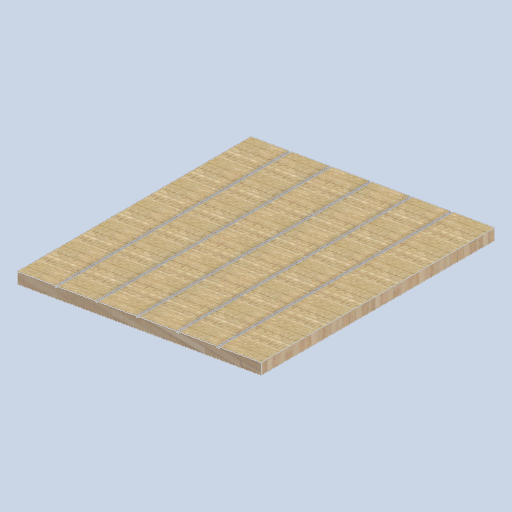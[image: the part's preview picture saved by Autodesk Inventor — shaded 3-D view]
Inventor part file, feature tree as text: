
AUTODESK INVENTOR PART (.ipt)
format: ipt  version: 2024.2 (Build 282272000, 272)  size: 427,520 bytes
history: native  units: mm
features: sketch x4, plane x3, extrude x2
ambient origin geometry x8: Origin, YZ Plane, XZ Plane, XY Plane, X Axis, Y Axis, Z Axis, Center Point
bodies: Solid1 (feature_tree)
feature tree (9):
  sketch  "Sketch1"  dims[d0=100.0mm d1=2108.0mm]
  plane  "Work Plane2"
  sketch  "Sketch2"  dims[d2=2200.0mm d3=13.962634mm]
  plane  "Work Plane3"
  extrude  "Extrusion1"  Depth=2108.0mm
  extrude  "Extrusion2"  Depth=2200.0mm
  plane  "Work Plane1"
  sketch  "Sketch3"  dims[d4=13.962634mm]
  sketch  "Sketch4"  dims[d5=2108.0mm d6=0.0mm d7=350.0mm d8=350.0mm d9=350.0mm d10=350.0mm d11=350.0mm d12=0.0mm d13=0.0mm]
